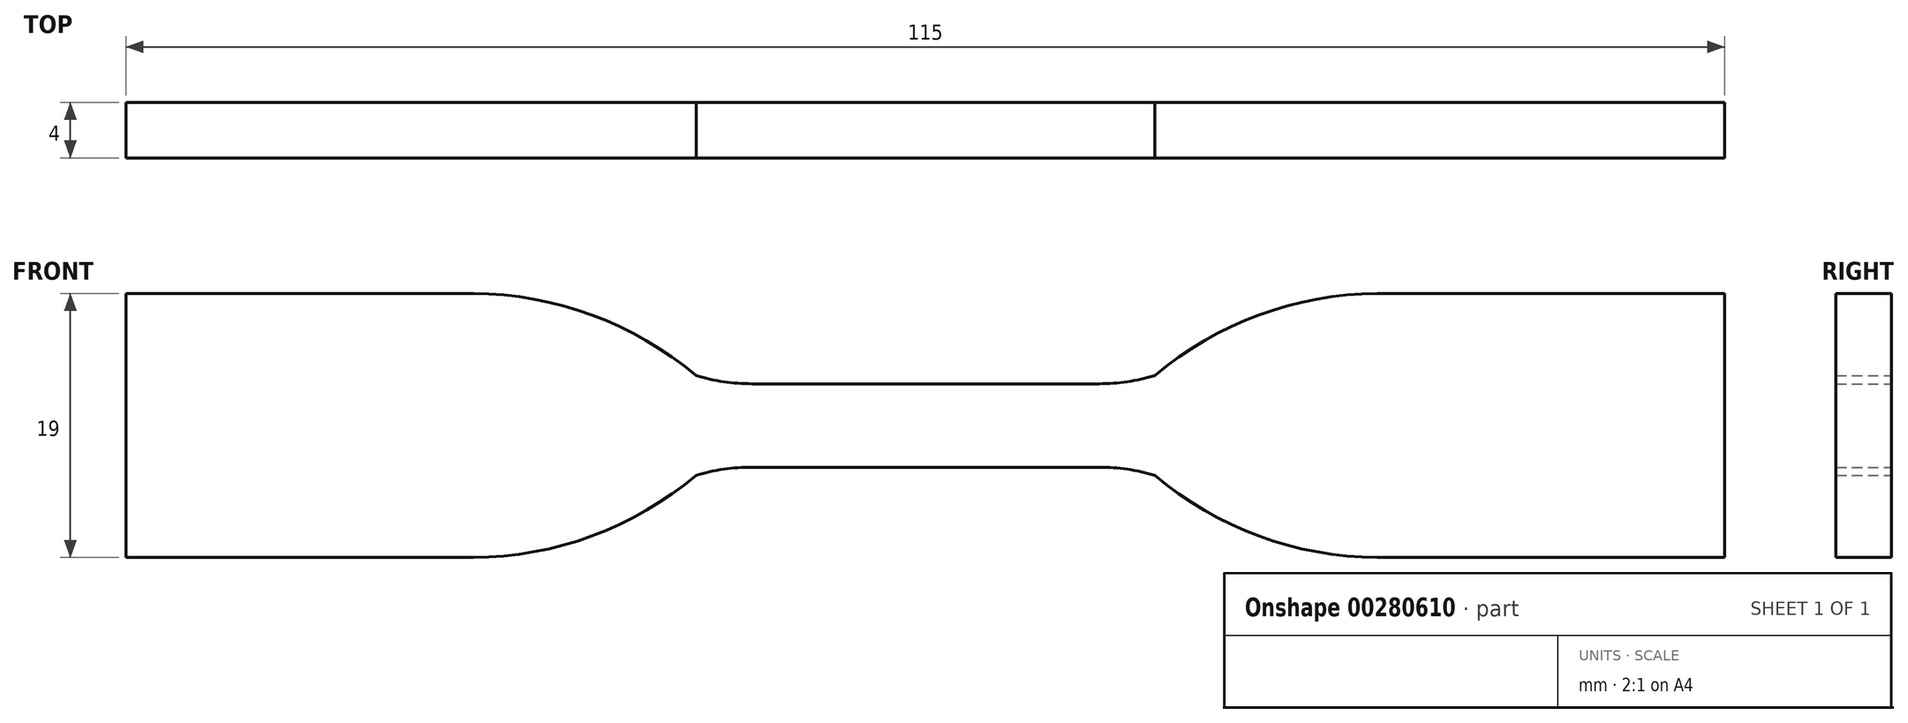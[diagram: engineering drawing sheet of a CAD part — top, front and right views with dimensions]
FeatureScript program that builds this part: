
annotation { "Feature Type Name" : "Feature", "Feature Type Description" : "" }
export const myFeature = defineFeature(function(context is Context, id is Id, definition is map)
    precondition{}
    {
        {
            var Q0;
            Q0=qCreatedBy(makeId("Front.planeOp"),FACE);
            var sketch = newSketch(context, id + "F0", { "sketchPlane" : qUnion([Q0])});
            skLineSegment(sketch, "E0", {"start": v(0, 3) * mm, "end": v(12.5, 3) * mm});
            skArc(sketch, "E1", {"start": v(12.5, 3) * mm, "mid": v(14.52, 3.15) * mm, "end": v(16.5, 3.58) * mm});
            skArc(sketch, "E2", {"start": v(32.5, 9.5) * mm, "mid": v(23.98, 7.95) * mm, "end": v(16.5, 3.58) * mm});
            skLineSegment(sketch, "E3", {"start": v(32.5, 9.5) * mm, "end": v(57.5, 9.5) * mm});
            skLineSegment(sketch, "E4.MirrorCS", {"start": v(32.5, -9.5) * mm, "end": v(57.5, -9.5) * mm});
            skLineSegment(sketch, "E5.MirrorCS", {"start": v(0, -3) * mm, "end": v(12.5, -3) * mm});
            skArc(sketch, "E6.MirrorCS", {"start": v(32.5, -9.5) * mm, "mid": v(23.98, -7.95) * mm, "end": v(16.5, -3.58) * mm});
            skArc(sketch, "E7.MirrorCS", {"start": v(12.5, -3) * mm, "mid": v(14.52, -3.15) * mm, "end": v(16.5, -3.58) * mm});
            skLineSegment(sketch, "E8.MirrorCS", {"start": v(-32.5, -9.5) * mm, "end": v(-57.5, -9.5) * mm});
            skArc(sketch, "E9.MirrorCS", {"start": v(-12.5, 3) * mm, "mid": v(-14.52, 3.15) * mm, "end": v(-16.5, 3.58) * mm});
            skLineSegment(sketch, "E10.MirrorCS", {"start": v(0, -3) * mm, "end": v(-12.5, -3) * mm});
            skArc(sketch, "E11.MirrorCS", {"start": v(-12.5, -3) * mm, "mid": v(-14.52, -3.15) * mm, "end": v(-16.5, -3.58) * mm});
            skLineSegment(sketch, "E12.MirrorCS", {"start": v(-32.5, 9.5) * mm, "end": v(-57.5, 9.5) * mm});
            skLineSegment(sketch, "E13.MirrorCS", {"start": v(0, 3) * mm, "end": v(-12.5, 3) * mm});
            skArc(sketch, "E14.MirrorCS", {"start": v(-32.5, -9.5) * mm, "mid": v(-23.98, -7.95) * mm, "end": v(-16.5, -3.58) * mm});
            skArc(sketch, "E15.MirrorCS", {"start": v(-32.5, 9.5) * mm, "mid": v(-23.98, 7.95) * mm, "end": v(-16.5, 3.58) * mm});
            skLineSegment(sketch, "E16", {"start": v(-57.5, -9.5) * mm, "end": v(-57.5, 9.5) * mm});
            skLineSegment(sketch, "E17", {"start": v(57.5, 9.5) * mm, "end": v(57.5, -9.5) * mm});
            skSolve(sketch);
        }
        {
            var Q0;
            Q0=makeQuery(id+"F0.imprint","IMPRINT",FACE,{"disambiguationData":[TD([[makeQuery(id+"F0.imprint","IMPRINT",EDGE,{"derivedFrom":sQuery(id+"F0.wireOp",EDGE,"E0")}),-1.0]])]});
            extrude(context, id + "F1", {"entities" : qUnion([Q0]), "endBound" : BoundingType.SYMMETRIC, "depth" : 4 * mm});
        }
    });
